# Revit family: Шкаф антивандальный настенный ШАН-Пенал ШАН-П
name_source: partatom
category: Обобщенные модели
units: mm (PartAtom-declared; Revit-internal decimal feet)

## family parameters
Всегда вертикально = Да
Может служить основой для арматурных стержней = Нет
На основе рабочей плоскости = Нет
Общий = Нет
При загрузке вырезать с полостями = Нет
Размер круглого соединителя = Использовать диаметр
Тип детали = Нормальный
Точка расчета площади = Нет

## types (2) — shared parameters
ADSK_URL документации изделия = https://www.ssd.ru
ADSK_URL страницы изделия = https://www.ssd.ru
ADSK_Единица измерения = шт.
ADSK_Завод-изготовитель = АО СВЯЗЬСРОЙДЕТАЛЬ
ADSK_Количество = 1
ADSK_Материал обозначение = Серый RAL 7035
ADSK_Размер_Глубина = 500 мм
ADSK_Размер_Ширина = 600 мм

## per-type parameters (varying)
| type | ADSK_Код изделия | ADSK_Масса_Текст | ADSK_Обозначение | ADSK_Размер_Высота | Высота двери | Высота крышки |
| Шкаф антивандальный настенный ШАН-Пенал ШАН-П 6U ССД | 130411-00469 | 17,0 | ШАН-П 6U (600x500мм) | 306 мм | 298 мм | 306 мм |
| Шкаф антивандальный настенный ШАН-Пенал ШАН-П 9U ССД | 130411-00470 | 21,3 | ШАН-П 9U (600x500мм) | 440 мм | 432 мм | 440 мм |

note: column(s) folded — value = type name in every type: ADSK_Наименование
